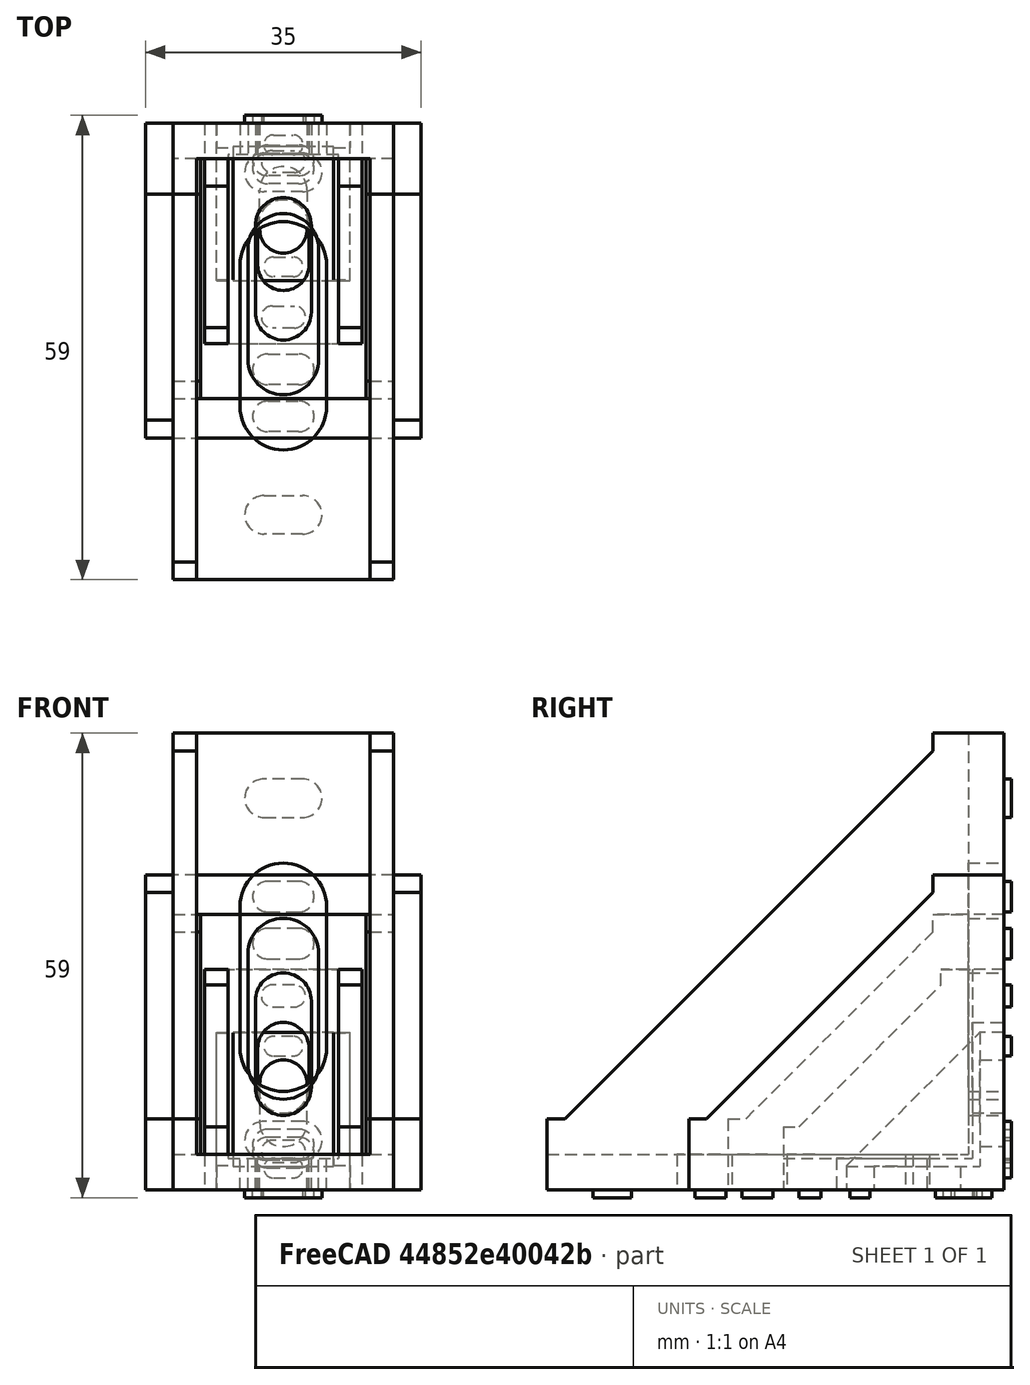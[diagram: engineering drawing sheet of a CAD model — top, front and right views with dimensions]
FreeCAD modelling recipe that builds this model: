
FCSTD DOCUMENT  (FreeCAD 0.21R30492 (Git))
Label: Corner_bracket
Comment: This model is licensed under CC-BY 4.0.\n\nDon´t forget to share your modifications with the community.
License: Creative Commons Attribution
LicenseURL: http://creativecommons.org/licenses/by/4.0/
objects: Sketcher::SketchObject×20, PartDesign::Pad×10, PartDesign::Pocket×10, Spreadsheet::Sheet×5, PartDesign::Plane×5, PartDesign::Mirrored×5, PartDesign::Body×5, App::Part×5, App::LinkGroup×4, App::Link×4
note: 75 computed .brp shape members not serialized (recipe doc carries the construction recipe); baked Part::Feature solids carry a one-line shape summary decoded from their .brp

FEATURE [Sketcher::SketchObject] Sketch
  FullyConstrained = true
  MapMode = 5
  Placement = pos=(0,0,0) rot=(0.57735,0.57735,0.57735;2.0944rad)
  Support = -> [YZ_Plane]
  expr: Constraints[10] = <<Spreadsheet>>.A_dim
  expr: Constraints[15] = <<Spreadsheet>>.D_aux2
  expr: Constraints[8] = <<Spreadsheet>>.A_dim
  expr: Constraints[9] = <<Spreadsheet>>.D_dim + <<Spreadsheet>>.D_aux1
  sketch-geometry (7):
    g0: LineSegment StartX=0 StartY=0 StartZ=0 EndX=0 EndY=35 EndZ=0
    g1: LineSegment StartX=0 StartY=35 StartZ=0 EndX=-9 EndY=35 EndZ=0
    g2: LineSegment StartX=-35 StartY=9 StartZ=0 EndX=-35 EndY=0 EndZ=0
    g3: LineSegment StartX=-35 StartY=0 StartZ=0 EndX=0 EndY=0 EndZ=0
    g4: LineSegment StartX=-35 StartY=9 StartZ=0 EndX=-32.75 EndY=9 EndZ=0
    g5: LineSegment StartX=-32.75 StartY=9 StartZ=0 EndX=-9 EndY=32.75 EndZ=0
    g6: LineSegment StartX=-9 StartY=32.75 StartZ=0 EndX=-9 EndY=35 EndZ=0
  constraints (20):
    c: Coincident(g-1,g0)
    c: PointOnObject(g0,g-2)
    c: Coincident(g0,g1)
    c: Horizontal(g1)
    c: PointOnObject(g2,g-1)
    c: Vertical(g2)
    c: Coincident(g2,g3)
    c: Coincident(g3,g0)
    c: DistanceY(g0,g0) = 35
    c: DistanceX(g1,g1) = 9
    c: DistanceX(g3,g3) = 35
    c: Coincident(g2,g4)
    c: Horizontal(g4)
    c: Coincident(g4,g5)
    c: Equal(g2,g1)
    c: DistanceX(g4,g4) = 2.25
    c: Angle(g5) = 0.785398
    c: Coincident(g6,g5)
    c: Coincident(g6,g1)
    c: Vertical(g6)
FEATURE [PartDesign::Pad] Pad
  Direction = (1,-2e-16,3e-16)
  Length = 28
  Length2 = 100
  Midplane = true
  Placement = pos=(0,0,0) rot=(0.57735,0.57735,0.57735;2.0944rad)
  Profile = -> Sketch
  ReferenceAxis = -> Sketch [N_Axis]
  Type = 0
  expr: Length = <<Spreadsheet>>.B_dim
FEATURE [Spreadsheet::Sheet] Spreadsheet
  cells = A1=Collection of Corner brackets to be used wth T slot Aluminum profiles; A2=Data from: various Aliexpress vendors; A5=Model; B5=Height; C5=Depth; D5=Width; E5=Internal space; F5=Thickness; G5=Slot height; H5=Slot length; I5=Pad width; J5=Slot diameter; K5=Daux1; L5=Daux2; M5=Al profile size; A6==hiddenref(Part.Model.String); B6(A_dim)==.B9; C6==.C9; D6(B_dim)==.D9; E6(C_dim)==.E9; F6(D_dim)==.F9; G6(E_dim)==.G9; H6(F_dim)==.H9; I6(G_dim)==.I9; J6(H_dim)==.J9; K6(D_aux1)==.K9; L6(D_aux2)==.L9; M6==.M9; A7=20x20; B7=20; C7==B7; D7=17; E7=12.8; F7=3; G7=8.5; H7=5; I7=5; J7=6; K7=0.1; L7=0.1; M7=20; A8=28x28; B8=28; C8==B8; D8=20; E8=14; F8=4; G8=13; H8=5; I8=5.6; J8=6.5; K8==F8; L8==0.5 * F8; M8=20; A9=30x30; B9=35; C9==B9; D9=28; E9=21; F9=4.5; G9=13; H9=11; I9=7.8; J9=7.1; K9==F9; L9==0.5 * F9; M9=30; A10=40x40; B10=40; C10==B10; D10=35; E10=28; F10=4.5; G10=16; H10=14; I10=7.8; J10=9; K10==F10; L10==0.5 * F10; M10=40; A11=58x58; B11=58; C11==B11; D11=28; E11=22; F11=4.5; G11=18; H11=18; I11=9.800000000000001; J11=11; K11==F11; L11==0.5 * F11; M11=30
  expr: .cells.Bind.B6.ZZ6 = tuple(.cells; <<B>> + str(hiddenref(Part.Model) + 7); <<ZZ>> + str(hiddenref(Part.Model) + 7))
FEATURE [Sketcher::SketchObject] Sketch001
  ExternalGeometry = -> [Pad]
  FullyConstrained = true
  MapMode = 5
  Placement = pos=(-1.36e-14,1.94e-14,35) rot=(0,0,-1;1.5708rad)
  Support = -> [Pad]
  expr: Constraints[10] = <<Spreadsheet>>.D_dim
  expr: Constraints[12] = <<Spreadsheet>>.C_dim
  sketch-geometry (5):
    g0: LineSegment StartX=35 StartY=-10.5 StartZ=0 EndX=35 EndY=10.5 EndZ=0
    g1: LineSegment StartX=35 StartY=10.5 StartZ=0 EndX=4.5 EndY=10.5 EndZ=0
    g2: LineSegment StartX=4.5 StartY=10.5 StartZ=0 EndX=4.5 EndY=-10.5 EndZ=0
    g3: LineSegment StartX=4.5 StartY=-10.5 StartZ=0 EndX=35 EndY=-10.5 EndZ=0
    g4: GeomPoint X=19.75 Y=0 Z=0
  constraints (13):
    c: Coincident(g0,g1)
    c: Coincident(g1,g2)
    c: Coincident(g2,g3)
    c: Coincident(g3,g0)
    c: Horizontal(g1)
    c: Horizontal(g3)
    c: Vertical(g0)
    c: Vertical(g2)
    c: Symmetric(g1,g0,g4)
    c: PointOnObject(g4,g-1)
    c: DistanceX(g1) = 4.5
    c: Vertical(g0,g-3)
    c: DistanceY(g0,g0) = 21
FEATURE [PartDesign::Pocket] Pocket
  BaseFeature = -> Pad
  Direction = (4e-16,-6e-16,-1)
  Length = 30.5
  Length2 = 5
  Placement = pos=(0,0,0) rot=(0.57735,0.57735,0.57735;2.0944rad)
  Profile = -> Sketch001
  ReferenceAxis = -> Sketch001 [N_Axis]
  Type = 0
  expr: Length = <<Spreadsheet>>.A_dim - <<Spreadsheet>>.D_dim
FEATURE [Sketcher::SketchObject] Sketch002
  FullyConstrained = true
  MapMode = 5
  Placement = pos=(0,0,0) rot=(1,0,0;1.5708rad)
  Support = -> [XZ_Plane]
  expr: Constraints[7] = <<Spreadsheet>>.E_dim
  expr: Constraints[8] = <<Spreadsheet>>.F_dim
  expr: Constraints[9] = <<Spreadsheet>>.H_dim
  sketch-geometry (4):
    g0: ArcOfCircle CenterX=0 CenterY=13 CenterZ=0 NormalX=0 NormalY=0 NormalZ=1 AngleXU=0 Radius=3.55 StartAngle=3.14159 EndAngle=6.28319
    g1: ArcOfCircle CenterX=0 CenterY=24 CenterZ=0 NormalX=0 NormalY=0 NormalZ=1 AngleXU=0 Radius=3.55 StartAngle=9.6e-15 EndAngle=3.14159
    g2: LineSegment StartX=3.55 StartY=13 StartZ=0 EndX=3.55 EndY=24 EndZ=0
    g3: LineSegment StartX=-3.55 StartY=24 StartZ=0 EndX=-3.55 EndY=13 EndZ=0
  constraints (10):
    c: Tangent(g0,g2) = -1.5708
    c: Tangent(g2,g1) = -1.5708
    c: Tangent(g1,g3) = -1.5708
    c: Tangent(g3,g0) = -1.5708
    c: Equal(g0,g1)
    c: PointOnObject(g0,g-2)
    c: PointOnObject(g1,g-2)
    c: DistanceY(g0) = 13
    c: DistanceY(g2,g2) = 11
    c: Diameter(g1) = 7.1
FEATURE [PartDesign::Pocket] Pocket001
  BaseFeature = -> Pocket
  Direction = (0,1,2e-16)
  Length = 5
  Length2 = 5
  Placement = pos=(0,0,0) rot=(0.57735,0.57735,0.57735;2.0944rad)
  Profile = -> Sketch002
  ReferenceAxis = -> Sketch002 [N_Axis]
  Reversed = true
  Type = 2
FEATURE [Sketcher::SketchObject] Sketch003
  FullyConstrained = true
  MapMode = 5
  Placement = pos=(0,0,0) rot=(1,0,0;1.5708rad)
  Support = -> [XZ_Plane]
  expr: Constraints[14] = <<Spreadsheet>>.G_dim / 2
  expr: Constraints[15] = <<Spreadsheet>>.G_dim / 4
  expr: Constraints[16] = (<<Spreadsheet>>.E_dim - <<Spreadsheet>>.H_dim / 2) / 2
  expr: Constraints[17] = (<<Spreadsheet>>.A_dim + <<Spreadsheet>>.E_dim + <<Spreadsheet>>.F_dim + <<Spreadsheet>>.H_dim / 2) / 2
  sketch-geometry (8):
    g0: ArcOfCircle CenterX=-1.95 CenterY=4.725 CenterZ=0 NormalX=0 NormalY=0 NormalZ=1 AngleXU=0 Radius=1.95 StartAngle=1.5708 EndAngle=4.71239
    g1: ArcOfCircle CenterX=1.95 CenterY=4.725 CenterZ=0 NormalX=0 NormalY=0 NormalZ=1 AngleXU=0 Radius=1.95 StartAngle=4.71239 EndAngle=7.85398
    g2: LineSegment StartX=-1.95 StartY=2.775 StartZ=0 EndX=1.95 EndY=2.775 EndZ=0
    g3: LineSegment StartX=1.95 StartY=6.675 StartZ=0 EndX=-1.95 EndY=6.675 EndZ=0
    g4: ArcOfCircle CenterX=-1.95 CenterY=31.275 CenterZ=0 NormalX=0 NormalY=0 NormalZ=1 AngleXU=0 Radius=1.95 StartAngle=1.5708 EndAngle=4.71239
    g5: ArcOfCircle CenterX=1.95 CenterY=31.275 CenterZ=0 NormalX=0 NormalY=0 NormalZ=1 AngleXU=0 Radius=1.95 StartAngle=4.71239 EndAngle=7.85398
    g6: LineSegment StartX=-1.95 StartY=29.325 StartZ=0 EndX=1.95 EndY=29.325 EndZ=0
    g7: LineSegment StartX=1.95 StartY=33.225 StartZ=0 EndX=-1.95 EndY=33.225 EndZ=0
  constraints (18):
    c: Tangent(g0,g2) = -1.5708
    c: Tangent(g2,g1) = -1.5708
    c: Tangent(g1,g3) = -1.5708
    c: Tangent(g3,g0) = -1.5708
    c: Equal(g0,g1)
    c: Tangent(g4,g6) = -1.5708
    c: Tangent(g6,g5) = -1.5708
    c: Tangent(g5,g7) = -1.5708
    c: Tangent(g7,g4) = -1.5708
    c: Equal(g4,g5)
    c: Symmetric(g1,g0,g-2)
    c: Symmetric(g4,g5,g-2)
    c: Equal(g7,g2)
    c: Equal(g1,g5)
    c: DistanceX(g7,g7) = 3.9
    c: Radius(g5) = 1.95
    c: DistanceY(g1) = 4.725
    c: DistanceY(g4) = 31.275
FEATURE [PartDesign::Pad] Pad001
  BaseFeature = -> Pocket001
  Direction = (0,-1,-2e-16)
  Length = 1
  Length2 = 10
  Placement = pos=(0,0,0) rot=(0.57735,0.57735,0.57735;2.0944rad)
  Profile = -> Sketch003
  ReferenceAxis = -> Sketch003 [N_Axis]
  Reversed = true
  Type = 0
FEATURE [PartDesign::Plane] DatumPlane
  AttachmentOffset = pos=(0,0,0) rot=(1,0,0;0.785398rad)
  Length = 63.0271
  MapMode = 5
  Placement = pos=(0,0,0) rot=(1,0,0;2.35619rad)
  ResizeMode = 0
  Support = -> [XZ_Plane]
  Width = 97.8799
FEATURE [PartDesign::Mirrored] Mirrored
  BaseFeature = -> Pad001
  MirrorPlane = -> DatumPlane
  Originals = -> [Pocket001,Pad001]
  Placement = pos=(0,0,0) rot=(0.57735,0.57735,0.57735;2.0944rad)
FEATURE [PartDesign::Body] Body  label="Corner bracket 35x35"
  Group = -> [Sketch,Pad,Sketch001,Pocket,Sketch002,Pocket001,Sketch003,Pad001,DatumPlane,Mirrored]
  Origin = -> Origin
  Tip = -> Mirrored
  expr: Label = <<Corner bracket %s>> % Spreadsheet.A_dim + <<x%s>> % Spreadsheet.A_dim
FEATURE [App::Part] Part  label="Corner bracket"
  Group = -> [Body]
  Model = 2
  Origin = -> Origin001
  Placement = pos=(0,0,0) rot=(0,0,1;0.523599rad)
  expr: .Model.Enum = Spreadsheet.cells[<<A7:|>>]
FEATURE [Spreadsheet::Sheet] Spreadsheet001
  cells = A1=Collection of Corner brackets to be used wth T slot Aluminum profiles; A2=Data from: various Aliexpress vendors; A5=Model; B5=Height; C5=Depth; D5=Width; E5=Internal space; F5=Thickness; G5=Slot height; H5=Slot length; I5=Pad width; J5=Slot diameter; K5=Daux1; L5=Daux2; M5=Al profile size; A6==hiddenref(Part001.Model.String); B6(A_dim)==.B7; C6==.C7; D6(B_dim)==.D7; E6(C_dim)==.E7; F6(D_dim)==.F7; G6(E_dim)==.G7; H6(F_dim)==.H7; I6(G_dim)==.I7; J6(H_dim)==.J7; K6(D_aux1)==.K7; L6(D_aux2)==.L7; M6==.M7; A7=20x20; B7=20; C7==B7; D7=17; E7=12.8; F7=3; G7=8.5; H7=5; I7=5; J7=6; K7=0.1; L7=0.1; M7=20; A8=28x28; B8=28; C8==B8; D8=20; E8=14; F8=4; G8=13; H8=5; I8=5.6; J8=6.5; K8==F8; L8==0.5 * F8; M8=20; A9=30x30; B9=35; C9==B9; D9=28; E9=21; F9=4.5; G9=13; H9=11; I9=7.8; J9=7.1; K9==F9; L9==0.5 * F9; M9=30; A10=40x40; B10=40; C10==B10; D10=35; E10=28; F10=4.5; G10=16; H10=14; I10=7.8; J10=9; K10==F10; L10==0.5 * F10; M10=40; A11=58x58; B11=58; C11==B11; D11=28; E11=22; F11=4.5; G11=18; H11=18; I11=9.800000000000001; J11=11; K11==F11; L11==0.5 * F11; M11=30
  expr: .cells.Bind.B6.ZZ6 = tuple(.cells; <<B>> + str(hiddenref(Part001.Model) + 7); <<ZZ>> + str(hiddenref(Part001.Model) + 7))
FEATURE [PartDesign::Plane] DatumPlane001
  AttachmentOffset = pos=(0,0,0) rot=(1,0,0;0.785398rad)
  Length = 65.3219
  MapMode = 5
  Placement = pos=(0,0,0) rot=(1,0,0;2.35619rad)
  ResizeMode = 0
  Support = -> [XZ_Plane003]
  Width = 132.702
FEATURE [Sketcher::SketchObject] Sketch004
  FullyConstrained = true
  MapMode = 5
  Placement = pos=(0,0,0) rot=(1,0,0;1.5708rad)
  Support = -> [XZ_Plane003]
  expr: Constraints[7] = <<Spreadsheet001>>.E_dim
  expr: Constraints[8] = <<Spreadsheet001>>.F_dim
  expr: Constraints[9] = <<Spreadsheet001>>.H_dim
  sketch-geometry (4):
    g0: ArcOfCircle CenterX=0 CenterY=8.5 CenterZ=0 NormalX=0 NormalY=0 NormalZ=1 AngleXU=0 Radius=3 StartAngle=3.14159 EndAngle=6.28319
    g1: ArcOfCircle CenterX=0 CenterY=13.5 CenterZ=0 NormalX=0 NormalY=0 NormalZ=1 AngleXU=0 Radius=3 StartAngle=0 EndAngle=3.14159
    g2: LineSegment StartX=3 StartY=8.5 StartZ=0 EndX=3 EndY=13.5 EndZ=0
    g3: LineSegment StartX=-3 StartY=13.5 StartZ=0 EndX=-3 EndY=8.5 EndZ=0
  constraints (10):
    c: Tangent(g0,g2) = -1.5708
    c: Tangent(g2,g1) = -1.5708
    c: Tangent(g1,g3) = -1.5708
    c: Tangent(g3,g0) = -1.5708
    c: Equal(g0,g1)
    c: PointOnObject(g0,g-2)
    c: PointOnObject(g1,g-2)
    c: DistanceY(g0) = 8.5
    c: DistanceY(g2,g2) = 5
    c: Diameter(g1) = 6
FEATURE [Sketcher::SketchObject] Sketch005
  FullyConstrained = true
  MapMode = 5
  Placement = pos=(0,0,0) rot=(0.57735,0.57735,0.57735;2.0944rad)
  Support = -> [YZ_Plane003]
  expr: Constraints[10] = <<Spreadsheet001>>.A_dim
  expr: Constraints[15] = <<Spreadsheet001>>.D_aux2
  expr: Constraints[8] = <<Spreadsheet001>>.A_dim
  expr: Constraints[9] = <<Spreadsheet001>>.D_dim + <<Spreadsheet001>>.D_aux1
  sketch-geometry (7):
    g0: LineSegment StartX=0 StartY=0 StartZ=0 EndX=0 EndY=20 EndZ=0
    g1: LineSegment StartX=0 StartY=20 StartZ=0 EndX=-3.1 EndY=20 EndZ=0
    g2: LineSegment StartX=-20 StartY=3.1 StartZ=0 EndX=-20 EndY=0 EndZ=0
    g3: LineSegment StartX=-20 StartY=0 StartZ=0 EndX=0 EndY=0 EndZ=0
    g4: LineSegment StartX=-20 StartY=3.1 StartZ=0 EndX=-19.9 EndY=3.1 EndZ=0
    g5: LineSegment StartX=-19.9 StartY=3.1 StartZ=0 EndX=-3.1 EndY=19.9 EndZ=0
    g6: LineSegment StartX=-3.1 StartY=19.9 StartZ=0 EndX=-3.1 EndY=20 EndZ=0
  constraints (20):
    c: Coincident(g-1,g0)
    c: PointOnObject(g0,g-2)
    c: Coincident(g0,g1)
    c: Horizontal(g1)
    c: PointOnObject(g2,g-1)
    c: Vertical(g2)
    c: Coincident(g2,g3)
    c: Coincident(g3,g0)
    c: DistanceY(g0,g0) = 20
    c: DistanceX(g1,g1) = 3.1
    c: DistanceX(g3,g3) = 20
    c: Coincident(g2,g4)
    c: Horizontal(g4)
    c: Coincident(g4,g5)
    c: Equal(g2,g1)
    c: DistanceX(g4,g4) = 0.1
    c: Angle(g5) = 0.785398
    c: Coincident(g6,g5)
    c: Coincident(g6,g1)
    c: Vertical(g6)
FEATURE [PartDesign::Pad] Pad002
  Direction = (1,-2e-16,3e-16)
  Length = 17
  Length2 = 100
  Midplane = true
  Placement = pos=(0,0,0) rot=(0.57735,0.57735,0.57735;2.0944rad)
  Profile = -> Sketch005
  ReferenceAxis = -> Sketch005 [N_Axis]
  Type = 0
  expr: Length = <<Spreadsheet001>>.B_dim
FEATURE [Sketcher::SketchObject] Sketch006
  ExternalGeometry = -> [Pad002]
  FullyConstrained = true
  MapMode = 5
  Placement = pos=(-7.8e-15,1.11e-14,20) rot=(0,0,-1;1.5708rad)
  Support = -> [Pad002]
  expr: Constraints[10] = <<Spreadsheet001>>.D_dim
  expr: Constraints[12] = <<Spreadsheet001>>.C_dim
  sketch-geometry (5):
    g0: LineSegment StartX=20 StartY=-6.4 StartZ=0 EndX=20 EndY=6.4 EndZ=0
    g1: LineSegment StartX=20 StartY=6.4 StartZ=0 EndX=3 EndY=6.4 EndZ=0
    g2: LineSegment StartX=3 StartY=6.4 StartZ=0 EndX=3 EndY=-6.4 EndZ=0
    g3: LineSegment StartX=3 StartY=-6.4 StartZ=0 EndX=20 EndY=-6.4 EndZ=0
    g4: GeomPoint X=11.5 Y=0 Z=0
  constraints (13):
    c: Coincident(g0,g1)
    c: Coincident(g1,g2)
    c: Coincident(g2,g3)
    c: Coincident(g3,g0)
    c: Horizontal(g1)
    c: Horizontal(g3)
    c: Vertical(g0)
    c: Vertical(g2)
    c: Symmetric(g1,g0,g4)
    c: PointOnObject(g4,g-1)
    c: DistanceX(g1) = 3
    c: Vertical(g0,g-3)
    c: DistanceY(g0,g0) = 12.8
FEATURE [PartDesign::Pocket] Pocket002
  BaseFeature = -> Pad002
  Direction = (4e-16,-6e-16,-1)
  Length = 17
  Length2 = 5
  Placement = pos=(0,0,0) rot=(0.57735,0.57735,0.57735;2.0944rad)
  Profile = -> Sketch006
  ReferenceAxis = -> Sketch006 [N_Axis]
  Type = 0
  expr: Length = <<Spreadsheet001>>.A_dim - <<Spreadsheet001>>.D_dim
FEATURE [PartDesign::Pocket] Pocket003
  BaseFeature = -> Pocket002
  Direction = (0,1,2e-16)
  Length = 5
  Length2 = 5
  Placement = pos=(0,0,0) rot=(0.57735,0.57735,0.57735;2.0944rad)
  Profile = -> Sketch004
  ReferenceAxis = -> Sketch004 [N_Axis]
  Reversed = true
  Type = 2
FEATURE [Sketcher::SketchObject] Sketch007
  FullyConstrained = true
  MapMode = 5
  Placement = pos=(0,0,0) rot=(1,0,0;1.5708rad)
  Support = -> [XZ_Plane003]
  expr: Constraints[14] = <<Spreadsheet001>>.G_dim / 2
  expr: Constraints[15] = <<Spreadsheet001>>.G_dim / 4
  expr: Constraints[16] = (<<Spreadsheet001>>.E_dim - <<Spreadsheet001>>.H_dim / 2) / 2
  expr: Constraints[17] = (<<Spreadsheet001>>.A_dim + <<Spreadsheet001>>.E_dim + <<Spreadsheet001>>.F_dim + <<Spreadsheet001>>.H_dim / 2) / 2
  sketch-geometry (8):
    g0: ArcOfCircle CenterX=-1.25 CenterY=2.75 CenterZ=0 NormalX=0 NormalY=0 NormalZ=1 AngleXU=0 Radius=1.25 StartAngle=1.5708 EndAngle=4.71239
    g1: ArcOfCircle CenterX=1.25 CenterY=2.75 CenterZ=0 NormalX=0 NormalY=0 NormalZ=1 AngleXU=0 Radius=1.25 StartAngle=4.71239 EndAngle=7.85398
    g2: LineSegment StartX=-1.25 StartY=1.5 StartZ=0 EndX=1.25 EndY=1.5 EndZ=0
    g3: LineSegment StartX=1.25 StartY=4 StartZ=0 EndX=-1.25 EndY=4 EndZ=0
    g4: ArcOfCircle CenterX=-1.25 CenterY=18.25 CenterZ=0 NormalX=0 NormalY=0 NormalZ=1 AngleXU=0 Radius=1.25 StartAngle=1.5708 EndAngle=4.71239
    g5: ArcOfCircle CenterX=1.25 CenterY=18.25 CenterZ=0 NormalX=0 NormalY=0 NormalZ=1 AngleXU=0 Radius=1.25 StartAngle=4.71239 EndAngle=7.85398
    g6: LineSegment StartX=-1.25 StartY=17 StartZ=0 EndX=1.25 EndY=17 EndZ=0
    g7: LineSegment StartX=1.25 StartY=19.5 StartZ=0 EndX=-1.25 EndY=19.5 EndZ=0
  constraints (18):
    c: Tangent(g0,g2) = -1.5708
    c: Tangent(g2,g1) = -1.5708
    c: Tangent(g1,g3) = -1.5708
    c: Tangent(g3,g0) = -1.5708
    c: Equal(g0,g1)
    c: Tangent(g4,g6) = -1.5708
    c: Tangent(g6,g5) = -1.5708
    c: Tangent(g5,g7) = -1.5708
    c: Tangent(g7,g4) = -1.5708
    c: Equal(g4,g5)
    c: Symmetric(g1,g0,g-2)
    c: Symmetric(g4,g5,g-2)
    c: Equal(g7,g2)
    c: Equal(g1,g5)
    c: DistanceX(g7,g7) = 2.5
    c: Radius(g5) = 1.25
    c: DistanceY(g1) = 2.75
    c: DistanceY(g4) = 18.25
FEATURE [PartDesign::Pad] Pad003
  BaseFeature = -> Pocket003
  Direction = (0,-1,-2e-16)
  Length = 1
  Length2 = 10
  Placement = pos=(0,0,0) rot=(0.57735,0.57735,0.57735;2.0944rad)
  Profile = -> Sketch007
  ReferenceAxis = -> Sketch007 [N_Axis]
  Reversed = true
  Type = 0
FEATURE [PartDesign::Mirrored] Mirrored001
  BaseFeature = -> Pad003
  MirrorPlane = -> DatumPlane001
  Originals = -> [Pocket003,Pad003]
  Placement = pos=(0,0,0) rot=(0.57735,0.57735,0.57735;2.0944rad)
FEATURE [PartDesign::Body] Body001  label="Corner bracket 20x20"
  Group = -> [Sketch005,Pad002,Sketch006,Pocket002,Sketch004,Pocket003,Sketch007,Pad003,DatumPlane001,Mirrored001]
  Origin = -> Origin003
  Tip = -> Mirrored001
  expr: Label = <<Corner bracket %s>> % Spreadsheet001.A_dim + <<x%s>> % Spreadsheet001.A_dim
FEATURE [App::Part] Part001  label="Corner bracket005"
  Group = -> [Body001]
  Model = 0
  Origin = -> Origin002
  expr: .Model.Enum = Spreadsheet001.cells[<<A7:|>>]
FEATURE [App::LinkGroup] CopyOnChangeGroup
  ElementList = -> [Part001,Body001,Origin003,XY_Plane003,Z_Axis003,Y_Axis003,X_Axis003,Mirrored001,Pad003,Sketch007,Pocket003,Pocket002,Sketch006,Pad002,Sketch005,YZ_Plane003,Sketch004,DatumPlane001,XZ_Plane003,Origin002,YZ_Plane002,XZ_Plane002,XY_Plane002,Z_Axis002,Y_Axis002,X_Axis002,Spreadsheet001]
  LinkMode = 1
FEATURE [App::Link] Link  label="Corner bracket001"
  LinkCopyOnChange = 2
  LinkCopyOnChangeGroup = -> CopyOnChangeGroup
  LinkCopyOnChangeSource = -> Part
  LinkCopyOnChangeTouched = true
  LinkPlacement = pos=(71,-7.7784e-06,0) rot=(0,0,1;0.261799rad)
  LinkedObject = -> Part001
  Model = 0
  Placement = pos=(71,-7.7784e-06,0) rot=(0,0,1;0.261799rad)
FEATURE [Spreadsheet::Sheet] Spreadsheet002
  cells = A1=Collection of Corner brackets to be used wth T slot Aluminum profiles; A2=Data from: various Aliexpress vendors; A5=Model; B5=Height; C5=Depth; D5=Width; E5=Internal space; F5=Thickness; G5=Slot height; H5=Slot length; I5=Pad width; J5=Slot diameter; K5=Daux1; L5=Daux2; M5=Al profile size; A6==hiddenref(Part002.Model.String); B6(A_dim)==.B8; C6==.C8; D6(B_dim)==.D8; E6(C_dim)==.E8; F6(D_dim)==.F8; G6(E_dim)==.G8; H6(F_dim)==.H8; I6(G_dim)==.I8; J6(H_dim)==.J8; K6(D_aux1)==.K8; L6(D_aux2)==.L8; M6==.M8; A7=20x20; B7=20; C7==B7; D7=17; E7=12.8; F7=3; G7=8.5; H7=5; I7=5; J7=6; K7=0.1; L7=0.1; M7=20; A8=28x28; B8=28; C8==B8; D8=20; E8=14; F8=4; G8=13; H8=5; I8=5.6; J8=6.5; K8==F8; L8==0.5 * F8; M8=20; A9=30x30; B9=35; C9==B9; D9=28; E9=21; F9=4.5; G9=13; H9=11; I9=7.8; J9=7.1; K9==F9; L9==0.5 * F9; M9=30; A10=40x40; B10=40; C10==B10; D10=35; E10=28; F10=4.5; G10=16; H10=14; I10=7.8; J10=9; K10==F10; L10==0.5 * F10; M10=40; A11=58x58; B11=58; C11==B11; D11=28; E11=22; F11=4.5; G11=18; H11=18; I11=9.800000000000001; J11=11; K11==F11; L11==0.5 * F11; M11=30
  expr: .cells.Bind.B6.ZZ6 = tuple(.cells; <<B>> + str(hiddenref(Part002.Model) + 7); <<ZZ>> + str(hiddenref(Part002.Model) + 7))
FEATURE [PartDesign::Plane] DatumPlane002
  AttachmentOffset = pos=(0,0,0) rot=(1,0,0;0.785398rad)
  Length = 65.3219
  MapMode = 5
  Placement = pos=(0,0,0) rot=(1,0,0;2.35619rad)
  ResizeMode = 0
  Support = -> [XZ_Plane005]
  Width = 132.702
FEATURE [Sketcher::SketchObject] Sketch008
  FullyConstrained = true
  MapMode = 5
  Placement = pos=(0,0,0) rot=(1,0,0;1.5708rad)
  Support = -> [XZ_Plane005]
  expr: Constraints[7] = <<Spreadsheet002>>.E_dim
  expr: Constraints[8] = <<Spreadsheet002>>.F_dim
  expr: Constraints[9] = <<Spreadsheet002>>.H_dim
  sketch-geometry (4):
    g0: ArcOfCircle CenterX=0 CenterY=13 CenterZ=0 NormalX=0 NormalY=0 NormalZ=1 AngleXU=0 Radius=3.25 StartAngle=3.14159 EndAngle=6.28319
    g1: ArcOfCircle CenterX=0 CenterY=18 CenterZ=0 NormalX=0 NormalY=0 NormalZ=1 AngleXU=0 Radius=3.25 StartAngle=7.603e-13 EndAngle=3.14159
    g2: LineSegment StartX=3.25 StartY=13 StartZ=0 EndX=3.25 EndY=18 EndZ=0
    g3: LineSegment StartX=-3.25 StartY=18 StartZ=0 EndX=-3.25 EndY=13 EndZ=0
  constraints (10):
    c: Tangent(g0,g2) = -1.5708
    c: Tangent(g2,g1) = -1.5708
    c: Tangent(g1,g3) = -1.5708
    c: Tangent(g3,g0) = -1.5708
    c: Equal(g0,g1)
    c: PointOnObject(g0,g-2)
    c: PointOnObject(g1,g-2)
    c: DistanceY(g0) = 13
    c: DistanceY(g2,g2) = 5
    c: Diameter(g1) = 6.5
FEATURE [Sketcher::SketchObject] Sketch009
  FullyConstrained = true
  MapMode = 5
  Placement = pos=(0,0,0) rot=(0.57735,0.57735,0.57735;2.0944rad)
  Support = -> [YZ_Plane005]
  expr: Constraints[10] = <<Spreadsheet002>>.A_dim
  expr: Constraints[15] = <<Spreadsheet002>>.D_aux2
  expr: Constraints[8] = <<Spreadsheet002>>.A_dim
  expr: Constraints[9] = <<Spreadsheet002>>.D_dim + <<Spreadsheet002>>.D_aux1
  sketch-geometry (7):
    g0: LineSegment StartX=0 StartY=0 StartZ=0 EndX=0 EndY=28 EndZ=0
    g1: LineSegment StartX=0 StartY=28 StartZ=0 EndX=-8 EndY=28 EndZ=0
    g2: LineSegment StartX=-28 StartY=8 StartZ=0 EndX=-28 EndY=0 EndZ=0
    g3: LineSegment StartX=-28 StartY=0 StartZ=0 EndX=0 EndY=0 EndZ=0
    g4: LineSegment StartX=-28 StartY=8 StartZ=0 EndX=-26 EndY=8 EndZ=0
    g5: LineSegment StartX=-26 StartY=8 StartZ=0 EndX=-8 EndY=26 EndZ=0
    g6: LineSegment StartX=-8 StartY=26 StartZ=0 EndX=-8 EndY=28 EndZ=0
  constraints (20):
    c: Coincident(g-1,g0)
    c: PointOnObject(g0,g-2)
    c: Coincident(g0,g1)
    c: Horizontal(g1)
    c: PointOnObject(g2,g-1)
    c: Vertical(g2)
    c: Coincident(g2,g3)
    c: Coincident(g3,g0)
    c: DistanceY(g0,g0) = 28
    c: DistanceX(g1,g1) = 8
    c: DistanceX(g3,g3) = 28
    c: Coincident(g2,g4)
    c: Horizontal(g4)
    c: Coincident(g4,g5)
    c: Equal(g2,g1)
    c: DistanceX(g4,g4) = 2
    c: Angle(g5) = 0.785398
    c: Coincident(g6,g5)
    c: Coincident(g6,g1)
    c: Vertical(g6)
FEATURE [PartDesign::Pad] Pad004
  Direction = (1,-2e-16,3e-16)
  Length = 20
  Length2 = 100
  Midplane = true
  Placement = pos=(0,0,0) rot=(0.57735,0.57735,0.57735;2.0944rad)
  Profile = -> Sketch009
  ReferenceAxis = -> Sketch009 [N_Axis]
  Type = 0
  expr: Length = <<Spreadsheet002>>.B_dim
FEATURE [Sketcher::SketchObject] Sketch010
  ExternalGeometry = -> [Pad004]
  FullyConstrained = true
  MapMode = 5
  Placement = pos=(-1.09e-14,1.55e-14,28) rot=(0,0,-1;1.5708rad)
  Support = -> [Pad004]
  expr: Constraints[10] = <<Spreadsheet002>>.D_dim
  expr: Constraints[12] = <<Spreadsheet002>>.C_dim
  sketch-geometry (5):
    g0: LineSegment StartX=28 StartY=-7 StartZ=0 EndX=28 EndY=7 EndZ=0
    g1: LineSegment StartX=28 StartY=7 StartZ=0 EndX=4 EndY=7 EndZ=0
    g2: LineSegment StartX=4 StartY=7 StartZ=0 EndX=4 EndY=-7 EndZ=0
    g3: LineSegment StartX=4 StartY=-7 StartZ=0 EndX=28 EndY=-7 EndZ=0
    g4: GeomPoint X=16 Y=0 Z=0
  constraints (13):
    c: Coincident(g0,g1)
    c: Coincident(g1,g2)
    c: Coincident(g2,g3)
    c: Coincident(g3,g0)
    c: Horizontal(g1)
    c: Horizontal(g3)
    c: Vertical(g0)
    c: Vertical(g2)
    c: Symmetric(g1,g0,g4)
    c: PointOnObject(g4,g-1)
    c: DistanceX(g1) = 4
    c: Vertical(g0,g-3)
    c: DistanceY(g0,g0) = 14
FEATURE [PartDesign::Pocket] Pocket004
  BaseFeature = -> Pad004
  Direction = (4e-16,-6e-16,-1)
  Length = 24
  Length2 = 5
  Placement = pos=(0,0,0) rot=(0.57735,0.57735,0.57735;2.0944rad)
  Profile = -> Sketch010
  ReferenceAxis = -> Sketch010 [N_Axis]
  Type = 0
  expr: Length = <<Spreadsheet002>>.A_dim - <<Spreadsheet002>>.D_dim
FEATURE [PartDesign::Pocket] Pocket005
  BaseFeature = -> Pocket004
  Direction = (0,1,2e-16)
  Length = 5
  Length2 = 5
  Placement = pos=(0,0,0) rot=(0.57735,0.57735,0.57735;2.0944rad)
  Profile = -> Sketch008
  ReferenceAxis = -> Sketch008 [N_Axis]
  Reversed = true
  Type = 2
FEATURE [Sketcher::SketchObject] Sketch011
  FullyConstrained = true
  MapMode = 5
  Placement = pos=(0,0,0) rot=(1,0,0;1.5708rad)
  Support = -> [XZ_Plane005]
  expr: Constraints[14] = <<Spreadsheet002>>.G_dim / 2
  expr: Constraints[15] = <<Spreadsheet002>>.G_dim / 4
  expr: Constraints[16] = (<<Spreadsheet002>>.E_dim - <<Spreadsheet002>>.H_dim / 2) / 2
  expr: Constraints[17] = (<<Spreadsheet002>>.A_dim + <<Spreadsheet002>>.E_dim + <<Spreadsheet002>>.F_dim + <<Spreadsheet002>>.H_dim / 2) / 2
  sketch-geometry (8):
    g0: ArcOfCircle CenterX=-1.4 CenterY=4.875 CenterZ=0 NormalX=0 NormalY=0 NormalZ=1 AngleXU=0 Radius=1.4 StartAngle=1.5708 EndAngle=4.71239
    g1: ArcOfCircle CenterX=1.4 CenterY=4.875 CenterZ=0 NormalX=0 NormalY=0 NormalZ=1 AngleXU=0 Radius=1.4 StartAngle=4.71239 EndAngle=7.85398
    g2: LineSegment StartX=-1.4 StartY=3.475 StartZ=0 EndX=1.4 EndY=3.475 EndZ=0
    g3: LineSegment StartX=1.4 StartY=6.275 StartZ=0 EndX=-1.4 EndY=6.275 EndZ=0
    g4: ArcOfCircle CenterX=-1.4 CenterY=24.625 CenterZ=0 NormalX=0 NormalY=0 NormalZ=1 AngleXU=0 Radius=1.4 StartAngle=1.5708 EndAngle=4.71239
    g5: ArcOfCircle CenterX=1.4 CenterY=24.625 CenterZ=0 NormalX=0 NormalY=0 NormalZ=1 AngleXU=0 Radius=1.4 StartAngle=4.71239 EndAngle=7.85398
    g6: LineSegment StartX=-1.4 StartY=23.225 StartZ=0 EndX=1.4 EndY=23.225 EndZ=0
    g7: LineSegment StartX=1.4 StartY=26.025 StartZ=0 EndX=-1.4 EndY=26.025 EndZ=0
  constraints (18):
    c: Tangent(g0,g2) = -1.5708
    c: Tangent(g2,g1) = -1.5708
    c: Tangent(g1,g3) = -1.5708
    c: Tangent(g3,g0) = -1.5708
    c: Equal(g0,g1)
    c: Tangent(g4,g6) = -1.5708
    c: Tangent(g6,g5) = -1.5708
    c: Tangent(g5,g7) = -1.5708
    c: Tangent(g7,g4) = -1.5708
    c: Equal(g4,g5)
    c: Symmetric(g1,g0,g-2)
    c: Symmetric(g4,g5,g-2)
    c: Equal(g7,g2)
    c: Equal(g1,g5)
    c: DistanceX(g7,g7) = 2.8
    c: Radius(g5) = 1.4
    c: DistanceY(g1) = 4.875
    c: DistanceY(g4) = 24.625
FEATURE [PartDesign::Pad] Pad005
  BaseFeature = -> Pocket005
  Direction = (0,-1,-2e-16)
  Length = 1
  Length2 = 10
  Placement = pos=(0,0,0) rot=(0.57735,0.57735,0.57735;2.0944rad)
  Profile = -> Sketch011
  ReferenceAxis = -> Sketch011 [N_Axis]
  Reversed = true
  Type = 0
FEATURE [PartDesign::Mirrored] Mirrored002
  BaseFeature = -> Pad005
  MirrorPlane = -> DatumPlane002
  Originals = -> [Pocket005,Pad005]
  Placement = pos=(0,0,0) rot=(0.57735,0.57735,0.57735;2.0944rad)
FEATURE [PartDesign::Body] Body002  label="Corner bracket 28x28"
  Group = -> [Sketch009,Pad004,Sketch010,Pocket004,Sketch008,Pocket005,Sketch011,Pad005,DatumPlane002,Mirrored002]
  Origin = -> Origin005
  Tip = -> Mirrored002
  expr: Label = <<Corner bracket %s>> % Spreadsheet002.A_dim + <<x%s>> % Spreadsheet002.A_dim
FEATURE [App::Part] Part002  label="Corner bracket006"
  Group = -> [Body002]
  Model = 1
  Origin = -> Origin004
  expr: .Model.Enum = Spreadsheet002.cells[<<A7:|>>]
FEATURE [App::LinkGroup] CopyOnChangeGroup001
  ElementList = -> [Part002,Body002,Origin005,XY_Plane005,Z_Axis005,Y_Axis005,X_Axis005,Mirrored002,Pad005,Sketch011,Pocket005,Pocket004,Sketch010,Pad004,Sketch009,YZ_Plane005,Sketch008,DatumPlane002,XZ_Plane005,Origin004,YZ_Plane004,XZ_Plane004,XY_Plane004,Z_Axis004,Y_Axis004,X_Axis004,Spreadsheet002]
  LinkMode = 1
FEATURE [App::Link] Link001  label="Corner bracket002"
  LinkCopyOnChange = 2
  LinkCopyOnChangeGroup = -> CopyOnChangeGroup001
  LinkCopyOnChangeSource = -> Part
  LinkCopyOnChangeTouched = true
  LinkPlacement = pos=(116.255,1.68256,1.2941) rot=(-0.437933,-0.117344,0.891316;0.584055rad)
  LinkedObject = -> Part002
  Model = 1
  Placement = pos=(116.255,1.68256,1.2941) rot=(-0.437933,-0.117344,0.891316;0.584055rad)
FEATURE [Spreadsheet::Sheet] Spreadsheet003
  cells = A1=Collection of Corner brackets to be used wth T slot Aluminum profiles; A2=Data from: various Aliexpress vendors; A5=Model; B5=Height; C5=Depth; D5=Width; E5=Internal space; F5=Thickness; G5=Slot height; H5=Slot length; I5=Pad width; J5=Slot diameter; K5=Daux1; L5=Daux2; M5=Al profile size; A6==hiddenref(Part003.Model.String); B6(A_dim)==.B11; C6==.C11; D6(B_dim)==.D11; E6(C_dim)==.E11; F6(D_dim)==.F11; G6(E_dim)==.G11; H6(F_dim)==.H11; I6(G_dim)==.I11; J6(H_dim)==.J11; K6(D_aux1)==.K11; L6(D_aux2)==.L11; M6==.M11; A7=20x20; B7=20; C7==B7; D7=17; E7=12.8; F7=3; G7=8.5; H7=5; I7=5; J7=6; K7=0.1; L7=0.1; M7=20; A8=28x28; B8=28; C8==B8; D8=20; E8=14; F8=4; G8=13; H8=5; I8=5.6; J8=6.5; K8==F8; L8==0.5 * F8; M8=20; A9=30x30; B9=35; C9==B9; D9=28; E9=21; F9=4.5; G9=13; H9=11; I9=7.8; J9=7.1; K9==F9; L9==0.5 * F9; M9=30; A10=40x40; B10=40; C10==B10; D10=35; E10=28; F10=4.5; G10=16; H10=14; I10=7.8; J10=9; K10==F10; L10==0.5 * F10; M10=40; A11=58x58; B11=58; C11==B11; D11=28; E11=22; F11=4.5; G11=18; H11=18; I11=9.800000000000001; J11=11; K11==F11; L11==0.5 * F11; M11=30
  expr: .cells.Bind.B6.ZZ6 = tuple(.cells; <<B>> + str(hiddenref(Part003.Model) + 7); <<ZZ>> + str(hiddenref(Part003.Model) + 7))
FEATURE [PartDesign::Plane] DatumPlane003
  AttachmentOffset = pos=(0,0,0) rot=(1,0,0;0.785398rad)
  Length = 63.0271
  MapMode = 5
  Placement = pos=(0,0,0) rot=(1,0,0;2.35619rad)
  ResizeMode = 0
  Support = -> [XZ_Plane007]
  Width = 97.8799
FEATURE [Sketcher::SketchObject] Sketch012
  FullyConstrained = true
  MapMode = 5
  Placement = pos=(0,0,0) rot=(1,0,0;1.5708rad)
  Support = -> [XZ_Plane007]
  expr: Constraints[7] = <<Spreadsheet003>>.E_dim
  expr: Constraints[8] = <<Spreadsheet003>>.F_dim
  expr: Constraints[9] = <<Spreadsheet003>>.H_dim
  sketch-geometry (4):
    g0: ArcOfCircle CenterX=0 CenterY=18 CenterZ=0 NormalX=0 NormalY=0 NormalZ=1 AngleXU=0 Radius=5.5 StartAngle=3.14159 EndAngle=6.28319
    g1: ArcOfCircle CenterX=0 CenterY=36 CenterZ=0 NormalX=0 NormalY=0 NormalZ=1 AngleXU=0 Radius=5.5 StartAngle=-5.3e-15 EndAngle=3.14159
    g2: LineSegment StartX=5.5 StartY=18 StartZ=0 EndX=5.5 EndY=36 EndZ=0
    g3: LineSegment StartX=-5.5 StartY=36 StartZ=0 EndX=-5.5 EndY=18 EndZ=0
  constraints (10):
    c: Tangent(g0,g2) = -1.5708
    c: Tangent(g2,g1) = -1.5708
    c: Tangent(g1,g3) = -1.5708
    c: Tangent(g3,g0) = -1.5708
    c: Equal(g0,g1)
    c: PointOnObject(g0,g-2)
    c: PointOnObject(g1,g-2)
    c: DistanceY(g0) = 18
    c: DistanceY(g2,g2) = 18
    c: Diameter(g1) = 11
FEATURE [Sketcher::SketchObject] Sketch013
  FullyConstrained = true
  MapMode = 5
  Placement = pos=(0,0,0) rot=(0.57735,0.57735,0.57735;2.0944rad)
  Support = -> [YZ_Plane007]
  expr: Constraints[10] = <<Spreadsheet003>>.A_dim
  expr: Constraints[15] = <<Spreadsheet003>>.D_aux2
  expr: Constraints[8] = <<Spreadsheet003>>.A_dim
  expr: Constraints[9] = <<Spreadsheet003>>.D_dim + <<Spreadsheet003>>.D_aux1
  sketch-geometry (7):
    g0: LineSegment StartX=0 StartY=0 StartZ=0 EndX=0 EndY=58 EndZ=0
    g1: LineSegment StartX=0 StartY=58 StartZ=0 EndX=-9 EndY=58 EndZ=0
    g2: LineSegment StartX=-58 StartY=9 StartZ=0 EndX=-58 EndY=0 EndZ=0
    g3: LineSegment StartX=-58 StartY=0 StartZ=0 EndX=0 EndY=0 EndZ=0
    g4: LineSegment StartX=-58 StartY=9 StartZ=0 EndX=-55.75 EndY=9 EndZ=0
    g5: LineSegment StartX=-55.75 StartY=9 StartZ=0 EndX=-9 EndY=55.75 EndZ=0
    g6: LineSegment StartX=-9 StartY=55.75 StartZ=0 EndX=-9 EndY=58 EndZ=0
  constraints (20):
    c: Coincident(g-1,g0)
    c: PointOnObject(g0,g-2)
    c: Coincident(g0,g1)
    c: Horizontal(g1)
    c: PointOnObject(g2,g-1)
    c: Vertical(g2)
    c: Coincident(g2,g3)
    c: Coincident(g3,g0)
    c: DistanceY(g0,g0) = 58
    c: DistanceX(g1,g1) = 9
    c: DistanceX(g3,g3) = 58
    c: Coincident(g2,g4)
    c: Horizontal(g4)
    c: Coincident(g4,g5)
    c: Equal(g2,g1)
    c: DistanceX(g4,g4) = 2.25
    c: Angle(g5) = 0.785398
    c: Coincident(g6,g5)
    c: Coincident(g6,g1)
    c: Vertical(g6)
FEATURE [PartDesign::Pad] Pad006
  Direction = (1,-2e-16,3e-16)
  Length = 28
  Length2 = 100
  Midplane = true
  Placement = pos=(0,0,0) rot=(0.57735,0.57735,0.57735;2.0944rad)
  Profile = -> Sketch013
  ReferenceAxis = -> Sketch013 [N_Axis]
  Type = 0
  expr: Length = <<Spreadsheet003>>.B_dim
FEATURE [Sketcher::SketchObject] Sketch014
  ExternalGeometry = -> [Pad006]
  FullyConstrained = true
  MapMode = 5
  Placement = pos=(-2.25e-14,3.22e-14,58) rot=(0,0,-1;1.5708rad)
  Support = -> [Pad006]
  expr: Constraints[10] = <<Spreadsheet003>>.D_dim
  expr: Constraints[12] = <<Spreadsheet003>>.C_dim
  sketch-geometry (5):
    g0: LineSegment StartX=58 StartY=-11 StartZ=0 EndX=58 EndY=11 EndZ=0
    g1: LineSegment StartX=58 StartY=11 StartZ=0 EndX=4.5 EndY=11 EndZ=0
    g2: LineSegment StartX=4.5 StartY=11 StartZ=0 EndX=4.5 EndY=-11 EndZ=0
    g3: LineSegment StartX=4.5 StartY=-11 StartZ=0 EndX=58 EndY=-11 EndZ=0
    g4: GeomPoint X=31.25 Y=0 Z=0
  constraints (13):
    c: Coincident(g0,g1)
    c: Coincident(g1,g2)
    c: Coincident(g2,g3)
    c: Coincident(g3,g0)
    c: Horizontal(g1)
    c: Horizontal(g3)
    c: Vertical(g0)
    c: Vertical(g2)
    c: Symmetric(g1,g0,g4)
    c: PointOnObject(g4,g-1)
    c: DistanceX(g1) = 4.5
    c: Vertical(g0,g-3)
    c: DistanceY(g0,g0) = 22
FEATURE [PartDesign::Pocket] Pocket006
  BaseFeature = -> Pad006
  Direction = (4e-16,-6e-16,-1)
  Length = 53.5
  Length2 = 5
  Placement = pos=(0,0,0) rot=(0.57735,0.57735,0.57735;2.0944rad)
  Profile = -> Sketch014
  ReferenceAxis = -> Sketch014 [N_Axis]
  Type = 0
  expr: Length = <<Spreadsheet003>>.A_dim - <<Spreadsheet003>>.D_dim
FEATURE [PartDesign::Pocket] Pocket007
  BaseFeature = -> Pocket006
  Direction = (0,1,2e-16)
  Length = 5
  Length2 = 5
  Placement = pos=(0,0,0) rot=(0.57735,0.57735,0.57735;2.0944rad)
  Profile = -> Sketch012
  ReferenceAxis = -> Sketch012 [N_Axis]
  Reversed = true
  Type = 2
FEATURE [Sketcher::SketchObject] Sketch015
  FullyConstrained = true
  MapMode = 5
  Placement = pos=(0,0,0) rot=(1,0,0;1.5708rad)
  Support = -> [XZ_Plane007]
  expr: Constraints[14] = <<Spreadsheet003>>.G_dim / 2
  expr: Constraints[15] = <<Spreadsheet003>>.G_dim / 4
  expr: Constraints[16] = (<<Spreadsheet003>>.E_dim - <<Spreadsheet003>>.H_dim / 2) / 2
  expr: Constraints[17] = (<<Spreadsheet003>>.A_dim + <<Spreadsheet003>>.E_dim + <<Spreadsheet003>>.F_dim + <<Spreadsheet003>>.H_dim / 2) / 2
  sketch-geometry (8):
    g0: ArcOfCircle CenterX=-2.45 CenterY=6.25 CenterZ=0 NormalX=0 NormalY=0 NormalZ=1 AngleXU=0 Radius=2.45 StartAngle=1.5708 EndAngle=4.71239
    g1: ArcOfCircle CenterX=2.45 CenterY=6.25 CenterZ=0 NormalX=0 NormalY=0 NormalZ=1 AngleXU=0 Radius=2.45 StartAngle=4.71239 EndAngle=7.85398
    g2: LineSegment StartX=-2.45 StartY=3.8 StartZ=0 EndX=2.45 EndY=3.8 EndZ=0
    g3: LineSegment StartX=2.45 StartY=8.7 StartZ=0 EndX=-2.45 EndY=8.7 EndZ=0
    g4: ArcOfCircle CenterX=-2.45 CenterY=49.75 CenterZ=0 NormalX=0 NormalY=0 NormalZ=1 AngleXU=0 Radius=2.45 StartAngle=1.5708 EndAngle=4.71239
    g5: ArcOfCircle CenterX=2.45 CenterY=49.75 CenterZ=0 NormalX=0 NormalY=0 NormalZ=1 AngleXU=0 Radius=2.45 StartAngle=4.71239 EndAngle=7.85398
    g6: LineSegment StartX=-2.45 StartY=47.3 StartZ=0 EndX=2.45 EndY=47.3 EndZ=0
    g7: LineSegment StartX=2.45 StartY=52.2 StartZ=0 EndX=-2.45 EndY=52.2 EndZ=0
  constraints (18):
    c: Tangent(g0,g2) = -1.5708
    c: Tangent(g2,g1) = -1.5708
    c: Tangent(g1,g3) = -1.5708
    c: Tangent(g3,g0) = -1.5708
    c: Equal(g0,g1)
    c: Tangent(g4,g6) = -1.5708
    c: Tangent(g6,g5) = -1.5708
    c: Tangent(g5,g7) = -1.5708
    c: Tangent(g7,g4) = -1.5708
    c: Equal(g4,g5)
    c: Symmetric(g1,g0,g-2)
    c: Symmetric(g4,g5,g-2)
    c: Equal(g7,g2)
    c: Equal(g1,g5)
    c: DistanceX(g7,g7) = 4.9
    c: Radius(g5) = 2.45
    c: DistanceY(g1) = 6.25
    c: DistanceY(g4) = 49.75
FEATURE [PartDesign::Pad] Pad007
  BaseFeature = -> Pocket007
  Direction = (0,-1,-2e-16)
  Length = 1
  Length2 = 10
  Placement = pos=(0,0,0) rot=(0.57735,0.57735,0.57735;2.0944rad)
  Profile = -> Sketch015
  ReferenceAxis = -> Sketch015 [N_Axis]
  Reversed = true
  Type = 0
FEATURE [PartDesign::Mirrored] Mirrored003
  BaseFeature = -> Pad007
  MirrorPlane = -> DatumPlane003
  Originals = -> [Pocket007,Pad007]
  Placement = pos=(0,0,0) rot=(0.57735,0.57735,0.57735;2.0944rad)
FEATURE [PartDesign::Body] Body003  label="Corner bracket 58x58"
  Group = -> [Sketch013,Pad006,Sketch014,Pocket006,Sketch012,Pocket007,Sketch015,Pad007,DatumPlane003,Mirrored003]
  Origin = -> Origin007
  Tip = -> Mirrored003
  expr: Label = <<Corner bracket %s>> % Spreadsheet003.A_dim + <<x%s>> % Spreadsheet003.A_dim
FEATURE [App::Part] Part003  label="Corner bracket007"
  Group = -> [Body003]
  Model = 4
  Origin = -> Origin006
  expr: .Model.Enum = Spreadsheet003.cells[<<A7:|>>]
FEATURE [App::LinkGroup] CopyOnChangeGroup002
  ElementList = -> [Part003,Body003,Origin007,XY_Plane007,Z_Axis007,Y_Axis007,X_Axis007,Mirrored003,Pad007,Sketch015,Pocket007,Pocket006,Sketch014,Pad006,Sketch013,YZ_Plane007,Sketch012,DatumPlane003,XZ_Plane007,Origin006,YZ_Plane006,XZ_Plane006,XY_Plane006,Z_Axis006,Y_Axis006,X_Axis006,Spreadsheet003]
  LinkMode = 1
FEATURE [App::Link] Link002  label="Corner bracket003"
  LinkCopyOnChange = 2
  LinkCopyOnChangeGroup = -> CopyOnChangeGroup002
  LinkCopyOnChangeSource = -> Part
  LinkCopyOnChangeTouched = true
  LinkPlacement = pos=(-5.00001,53,0) rot=(0,0,1;1.309rad)
  LinkedObject = -> Part003
  Model = 4
  Placement = pos=(-5.00001,53,0) rot=(0,0,1;1.309rad)
FEATURE [Spreadsheet::Sheet] Spreadsheet004
  cells = A1=Collection of Corner brackets to be used wth T slot Aluminum profiles; A2=Data from: various Aliexpress vendors; A5=Model; B5=Height; C5=Depth; D5=Width; E5=Internal space; F5=Thickness; G5=Slot height; H5=Slot length; I5=Pad width; J5=Slot diameter; K5=Daux1; L5=Daux2; M5=Al profile size; A6==hiddenref(Part004.Model.String); B6(A_dim)==.B10; C6==.C10; D6(B_dim)==.D10; E6(C_dim)==.E10; F6(D_dim)==.F10; G6(E_dim)==.G10; H6(F_dim)==.H10; I6(G_dim)==.I10; J6(H_dim)==.J10; K6(D_aux1)==.K10; L6(D_aux2)==.L10; M6==.M10; A7=20x20; B7=20; C7==B7; D7=17; E7=12.8; F7=3; G7=8.5; H7=5; I7=5; J7=6; K7=0.1; L7=0.1; M7=20; A8=28x28; B8=28; C8==B8; D8=20; E8=14; F8=4; G8=13; H8=5; I8=5.6; J8=6.5; K8==F8; L8==0.5 * F8; M8=20; A9=30x30; B9=35; C9==B9; D9=28; E9=21; F9=4.5; G9=13; H9=11; I9=7.8; J9=7.1; K9==F9; L9==0.5 * F9; M9=30; A10=40x40; B10=40; C10==B10; D10=35; E10=28; F10=4.5; G10=16; H10=14; I10=7.8; J10=9; K10==F10; L10==0.5 * F10; M10=40; A11=58x58; B11=58; C11==B11; D11=28; E11=22; F11=4.5; G11=18; H11=18; I11=9.800000000000001; J11=11; K11==F11; L11==0.5 * F11; M11=30
  expr: .cells.Bind.B6.ZZ6 = tuple(.cells; <<B>> + str(hiddenref(Part004.Model) + 7); <<ZZ>> + str(hiddenref(Part004.Model) + 7))
FEATURE [PartDesign::Plane] DatumPlane004
  AttachmentOffset = pos=(0,0,0) rot=(1,0,0;0.785398rad)
  Length = 63.0271
  MapMode = 5
  Placement = pos=(0,0,0) rot=(1,0,0;2.35619rad)
  ResizeMode = 0
  Support = -> [XZ_Plane009]
  Width = 97.8799
FEATURE [Sketcher::SketchObject] Sketch016
  FullyConstrained = true
  MapMode = 5
  Placement = pos=(0,0,0) rot=(1,0,0;1.5708rad)
  Support = -> [XZ_Plane009]
  expr: Constraints[7] = <<Spreadsheet004>>.E_dim
  expr: Constraints[8] = <<Spreadsheet004>>.F_dim
  expr: Constraints[9] = <<Spreadsheet004>>.H_dim
  sketch-geometry (4):
    g0: ArcOfCircle CenterX=0 CenterY=16 CenterZ=0 NormalX=0 NormalY=0 NormalZ=1 AngleXU=0 Radius=4.5 StartAngle=3.14159 EndAngle=6.28319
    g1: ArcOfCircle CenterX=0 CenterY=30 CenterZ=0 NormalX=0 NormalY=0 NormalZ=1 AngleXU=0 Radius=4.5 StartAngle=4.0227e-12 EndAngle=3.14159
    g2: LineSegment StartX=4.5 StartY=16 StartZ=0 EndX=4.5 EndY=30 EndZ=0
    g3: LineSegment StartX=-4.5 StartY=30 StartZ=0 EndX=-4.5 EndY=16 EndZ=0
  constraints (10):
    c: Tangent(g0,g2) = -1.5708
    c: Tangent(g2,g1) = -1.5708
    c: Tangent(g1,g3) = -1.5708
    c: Tangent(g3,g0) = -1.5708
    c: Equal(g0,g1)
    c: PointOnObject(g0,g-2)
    c: PointOnObject(g1,g-2)
    c: DistanceY(g0) = 16
    c: DistanceY(g2,g2) = 14
    c: Diameter(g1) = 9
FEATURE [Sketcher::SketchObject] Sketch017
  FullyConstrained = true
  MapMode = 5
  Placement = pos=(0,0,0) rot=(0.57735,0.57735,0.57735;2.0944rad)
  Support = -> [YZ_Plane009]
  expr: Constraints[10] = <<Spreadsheet004>>.A_dim
  expr: Constraints[15] = <<Spreadsheet004>>.D_aux2
  expr: Constraints[8] = <<Spreadsheet004>>.A_dim
  expr: Constraints[9] = <<Spreadsheet004>>.D_dim + <<Spreadsheet004>>.D_aux1
  sketch-geometry (7):
    g0: LineSegment StartX=0 StartY=0 StartZ=0 EndX=0 EndY=40 EndZ=0
    g1: LineSegment StartX=0 StartY=40 StartZ=0 EndX=-9 EndY=40 EndZ=0
    g2: LineSegment StartX=-40 StartY=9 StartZ=0 EndX=-40 EndY=0 EndZ=0
    g3: LineSegment StartX=-40 StartY=0 StartZ=0 EndX=0 EndY=0 EndZ=0
    g4: LineSegment StartX=-40 StartY=9 StartZ=0 EndX=-37.75 EndY=9 EndZ=0
    g5: LineSegment StartX=-37.75 StartY=9 StartZ=0 EndX=-9 EndY=37.75 EndZ=0
    g6: LineSegment StartX=-9 StartY=37.75 StartZ=0 EndX=-9 EndY=40 EndZ=0
  constraints (20):
    c: Coincident(g-1,g0)
    c: PointOnObject(g0,g-2)
    c: Coincident(g0,g1)
    c: Horizontal(g1)
    c: PointOnObject(g2,g-1)
    c: Vertical(g2)
    c: Coincident(g2,g3)
    c: Coincident(g3,g0)
    c: DistanceY(g0,g0) = 40
    c: DistanceX(g1,g1) = 9
    c: DistanceX(g3,g3) = 40
    c: Coincident(g2,g4)
    c: Horizontal(g4)
    c: Coincident(g4,g5)
    c: Equal(g2,g1)
    c: DistanceX(g4,g4) = 2.25
    c: Angle(g5) = 0.785398
    c: Coincident(g6,g5)
    c: Coincident(g6,g1)
    c: Vertical(g6)
FEATURE [PartDesign::Pad] Pad008
  Direction = (1,-2e-16,3e-16)
  Length = 35
  Length2 = 100
  Midplane = true
  Placement = pos=(0,0,0) rot=(0.57735,0.57735,0.57735;2.0944rad)
  Profile = -> Sketch017
  ReferenceAxis = -> Sketch017 [N_Axis]
  Type = 0
  expr: Length = <<Spreadsheet004>>.B_dim
FEATURE [Sketcher::SketchObject] Sketch018
  ExternalGeometry = -> [Pad008]
  FullyConstrained = true
  MapMode = 5
  Placement = pos=(-1.55e-14,2.22e-14,40) rot=(0,0,-1;1.5708rad)
  Support = -> [Pad008]
  expr: Constraints[10] = <<Spreadsheet004>>.D_dim
  expr: Constraints[12] = <<Spreadsheet004>>.C_dim
  sketch-geometry (5):
    g0: LineSegment StartX=40 StartY=-14 StartZ=0 EndX=40 EndY=14 EndZ=0
    g1: LineSegment StartX=40 StartY=14 StartZ=0 EndX=4.5 EndY=14 EndZ=0
    g2: LineSegment StartX=4.5 StartY=14 StartZ=0 EndX=4.5 EndY=-14 EndZ=0
    g3: LineSegment StartX=4.5 StartY=-14 StartZ=0 EndX=40 EndY=-14 EndZ=0
    g4: GeomPoint X=22.25 Y=0 Z=0
  constraints (13):
    c: Coincident(g0,g1)
    c: Coincident(g1,g2)
    c: Coincident(g2,g3)
    c: Coincident(g3,g0)
    c: Horizontal(g1)
    c: Horizontal(g3)
    c: Vertical(g0)
    c: Vertical(g2)
    c: Symmetric(g1,g0,g4)
    c: PointOnObject(g4,g-1)
    c: DistanceX(g1) = 4.5
    c: Vertical(g0,g-3)
    c: DistanceY(g0,g0) = 28
FEATURE [PartDesign::Pocket] Pocket008
  BaseFeature = -> Pad008
  Direction = (4e-16,-6e-16,-1)
  Length = 35.5
  Length2 = 5
  Placement = pos=(0,0,0) rot=(0.57735,0.57735,0.57735;2.0944rad)
  Profile = -> Sketch018
  ReferenceAxis = -> Sketch018 [N_Axis]
  Type = 0
  expr: Length = <<Spreadsheet004>>.A_dim - <<Spreadsheet004>>.D_dim
FEATURE [PartDesign::Pocket] Pocket009
  BaseFeature = -> Pocket008
  Direction = (0,1,2e-16)
  Length = 5
  Length2 = 5
  Placement = pos=(0,0,0) rot=(0.57735,0.57735,0.57735;2.0944rad)
  Profile = -> Sketch016
  ReferenceAxis = -> Sketch016 [N_Axis]
  Reversed = true
  Type = 2
FEATURE [Sketcher::SketchObject] Sketch019
  FullyConstrained = true
  MapMode = 5
  Placement = pos=(0,0,0) rot=(1,0,0;1.5708rad)
  Support = -> [XZ_Plane009]
  expr: Constraints[14] = <<Spreadsheet004>>.G_dim / 2
  expr: Constraints[15] = <<Spreadsheet004>>.G_dim / 4
  expr: Constraints[16] = (<<Spreadsheet004>>.E_dim - <<Spreadsheet004>>.H_dim / 2) / 2
  expr: Constraints[17] = (<<Spreadsheet004>>.A_dim + <<Spreadsheet004>>.E_dim + <<Spreadsheet004>>.F_dim + <<Spreadsheet004>>.H_dim / 2) / 2
  sketch-geometry (8):
    g0: ArcOfCircle CenterX=-1.95 CenterY=5.75 CenterZ=0 NormalX=0 NormalY=0 NormalZ=1 AngleXU=0 Radius=1.95 StartAngle=1.5708 EndAngle=4.71239
    g1: ArcOfCircle CenterX=1.95 CenterY=5.75 CenterZ=0 NormalX=0 NormalY=0 NormalZ=1 AngleXU=0 Radius=1.95 StartAngle=4.71239 EndAngle=7.85398
    g2: LineSegment StartX=-1.95 StartY=3.8 StartZ=0 EndX=1.95 EndY=3.8 EndZ=0
    g3: LineSegment StartX=1.95 StartY=7.7 StartZ=0 EndX=-1.95 EndY=7.7 EndZ=0
    g4: ArcOfCircle CenterX=-1.95 CenterY=37.25 CenterZ=0 NormalX=0 NormalY=0 NormalZ=1 AngleXU=0 Radius=1.95 StartAngle=1.5708 EndAngle=4.71239
    g5: ArcOfCircle CenterX=1.95 CenterY=37.25 CenterZ=0 NormalX=0 NormalY=0 NormalZ=1 AngleXU=0 Radius=1.95 StartAngle=4.71239 EndAngle=7.85398
    g6: LineSegment StartX=-1.95 StartY=35.3 StartZ=0 EndX=1.95 EndY=35.3 EndZ=0
    g7: LineSegment StartX=1.95 StartY=39.2 StartZ=0 EndX=-1.95 EndY=39.2 EndZ=0
  constraints (18):
    c: Tangent(g0,g2) = -1.5708
    c: Tangent(g2,g1) = -1.5708
    c: Tangent(g1,g3) = -1.5708
    c: Tangent(g3,g0) = -1.5708
    c: Equal(g0,g1)
    c: Tangent(g4,g6) = -1.5708
    c: Tangent(g6,g5) = -1.5708
    c: Tangent(g5,g7) = -1.5708
    c: Tangent(g7,g4) = -1.5708
    c: Equal(g4,g5)
    c: Symmetric(g1,g0,g-2)
    c: Symmetric(g4,g5,g-2)
    c: Equal(g7,g2)
    c: Equal(g1,g5)
    c: DistanceX(g7,g7) = 3.9
    c: Radius(g5) = 1.95
    c: DistanceY(g1) = 5.75
    c: DistanceY(g4) = 37.25
FEATURE [PartDesign::Pad] Pad009
  BaseFeature = -> Pocket009
  Direction = (0,-1,-2e-16)
  Length = 1
  Length2 = 10
  Placement = pos=(0,0,0) rot=(0.57735,0.57735,0.57735;2.0944rad)
  Profile = -> Sketch019
  ReferenceAxis = -> Sketch019 [N_Axis]
  Reversed = true
  Type = 0
FEATURE [PartDesign::Mirrored] Mirrored004
  BaseFeature = -> Pad009
  MirrorPlane = -> DatumPlane004
  Originals = -> [Pocket009,Pad009]
  Placement = pos=(0,0,0) rot=(0.57735,0.57735,0.57735;2.0944rad)
FEATURE [PartDesign::Body] Body004  label="Corner bracket 40x041"
  Group = -> [Sketch017,Pad008,Sketch018,Pocket008,Sketch016,Pocket009,Sketch019,Pad009,DatumPlane004,Mirrored004]
  Origin = -> Origin009
  Tip = -> Mirrored004
  expr: Label = <<Corner bracket %s>> % Spreadsheet004.A_dim + <<x%s>> % Spreadsheet004.A_dim
FEATURE [App::Part] Part004  label="Corner bracket008"
  Group = -> [Body004]
  Model = 3
  Origin = -> Origin008
  expr: .Model.Enum = Spreadsheet004.cells[<<A7:|>>]
FEATURE [App::LinkGroup] CopyOnChangeGroup003
  ElementList = -> [Part004,Body004,Origin009,XY_Plane009,Z_Axis009,Y_Axis009,X_Axis009,Mirrored004,Pad009,Sketch019,Pocket009,Pocket008,Sketch018,Pad008,Sketch017,YZ_Plane009,Sketch016,DatumPlane004,XZ_Plane009,Origin008,YZ_Plane008,XZ_Plane008,XY_Plane008,Z_Axis008,Y_Axis008,X_Axis008,Spreadsheet004]
  LinkMode = 1
FEATURE [App::Link] Link003  label="Corner bracket004"
  LinkCopyOnChange = 2
  LinkCopyOnChangeGroup = -> CopyOnChangeGroup003
  LinkCopyOnChangeSource = -> Part
  LinkCopyOnChangeTouched = true
  LinkPlacement = pos=(106,48,25) rot=(0,0,1;1.0472rad)
  LinkedObject = -> Part004
  Model = 3
  Placement = pos=(106,48,25) rot=(0,0,1;1.0472rad)
